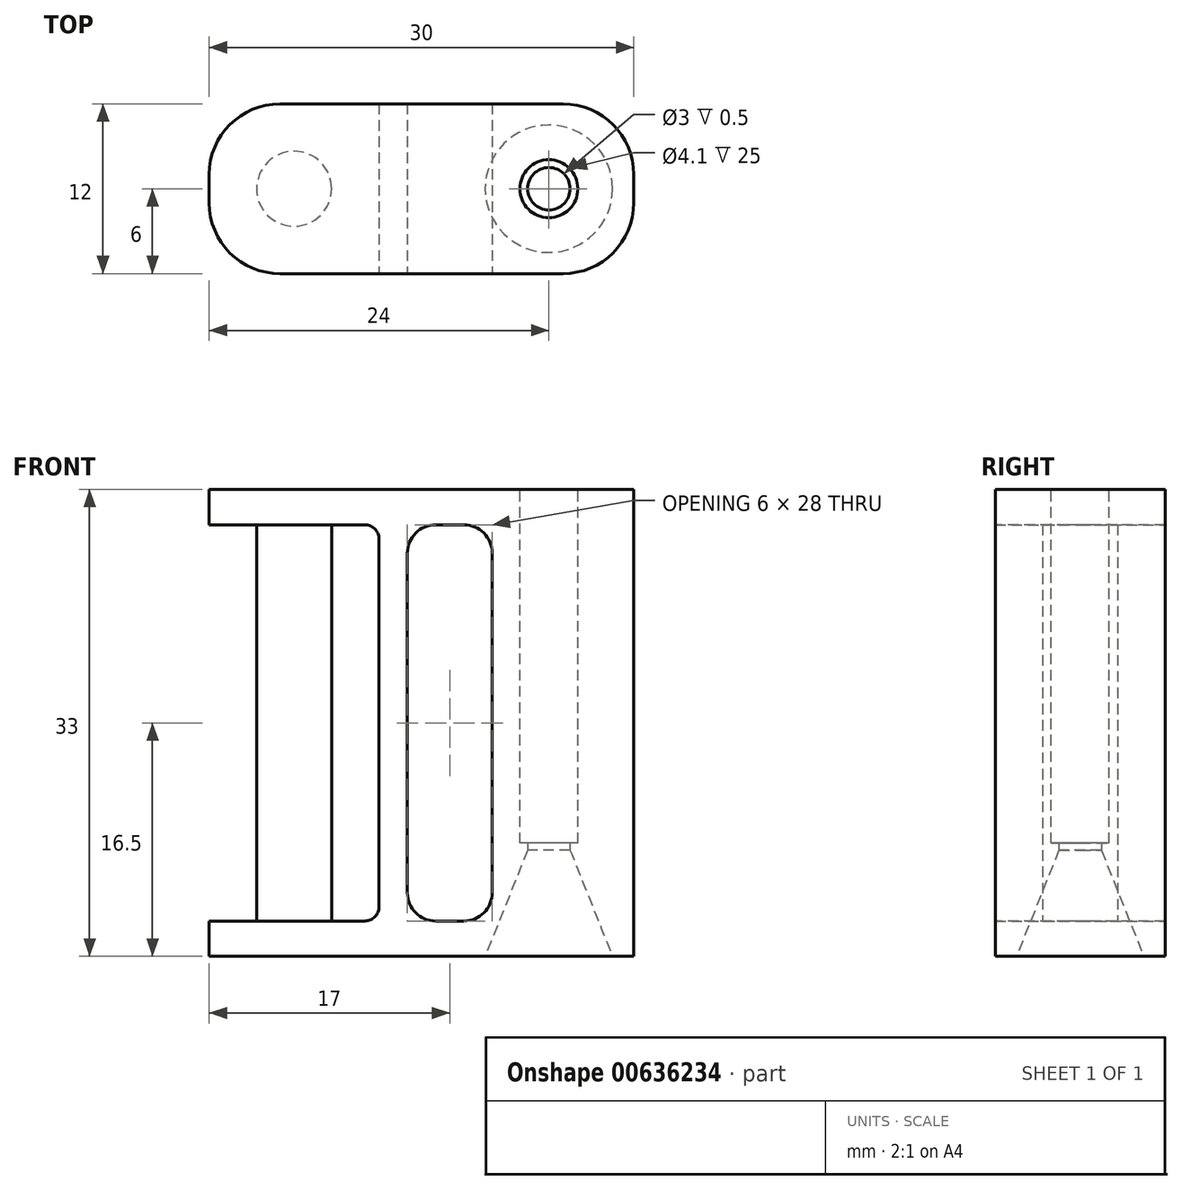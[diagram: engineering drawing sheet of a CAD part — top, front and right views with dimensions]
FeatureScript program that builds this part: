
annotation { "Feature Type Name" : "Feature", "Feature Type Description" : "" }
export const myFeature = defineFeature(function(context is Context, id is Id, definition is map)
    precondition{}
    {
        {
            var Q0;
            Q0=qCreatedBy(makeId("Top.planeOp"),FACE);
            var sketch = newSketch(context, id + "F0", { "sketchPlane" : qUnion([Q0])});
            skLineSegment(sketch, "E0.bottom", {"start": v(0, 0) * mm, "end": v(30, 0) * mm});
            skLineSegment(sketch, "E0.top", {"start": v(0, 12) * mm, "end": v(30, 12) * mm});
            skLineSegment(sketch, "E0.left", {"start": v(0, 0) * mm, "end": v(0, 12) * mm});
            skLineSegment(sketch, "E0.right", {"start": v(30, 0) * mm, "end": v(30, 12) * mm});
            skCircle(sketch, "E1", {"center": v(24, 6) * mm, "radius": 1.5 * mm});
            skSolve(sketch);
        }
        {
            var Q0;
            Q0=makeQuery(id+"F0.imprint","IMPRINT",FACE,{"disambiguationData":[TD([[makeQuery(id+"F0.imprint","IMPRINT",EDGE,{"derivedFrom":sQuery(id+"F0.wireOp",EDGE,"E0.bottom")}),1.0]])]});
            extrude(context, id + "F1", {"entities" : qUnion([Q0]), "depth" : 33 * mm, "offsetDistance" : 25 * mm});
        }
        {
            var Q0;
            Q0=makeQuery(id+"F1.opExtrude","SWEPT_FACE",FACE,{"disambiguationData":[OSD([sQuery(id+"F0.wireOp",EDGE,"E0.bottom")])]});
            var sketch = newSketch(context, id + "F2", { "sketchPlane" : qUnion([Q0])});
            skLineSegment(sketch, "E2.bottom", {"start": v(0, 30.5) * mm, "end": v(12, 30.5) * mm});
            skLineSegment(sketch, "E2.top", {"start": v(0, 2.5) * mm, "end": v(12, 2.5) * mm});
            skLineSegment(sketch, "E2.left", {"start": v(0, 30.5) * mm, "end": v(0, 2.5) * mm});
            skLineSegment(sketch, "E2.right", {"start": v(12, 30.5) * mm, "end": v(12, 2.5) * mm});
            skSolve(sketch);
        }
        {
            var Q0;
            Q0=makeQuery(id+"F2.imprint","IMPRINT",FACE,{"disambiguationData":[TD([[makeQuery(id+"F2.imprint","IMPRINT",EDGE,{"derivedFrom":sQuery(id+"F2.wireOp",EDGE,"E2.bottom")}),-1.0]])]});
            extrude(context, id + "F3", {"entities" : qUnion([Q0]), "operationType" : NewBodyOperationType.REMOVE, "oppositeDirection" : true, "depth" : 25 * mm, "offsetDistance" : 25 * mm});
        }
        {
            var Q0;
            Q0=makeQuery(id+"F3.boolean.opBoolean","COPY",FACE,{"derivedFrom":makeQuery(id+"F3.opExtrude","SWEPT_FACE",FACE,{"disambiguationData":[OSD([sQuery(id+"F2.wireOp",EDGE,"E2.top")])]})});
            var sketch = newSketch(context, id + "F4", { "sketchPlane" : qUnion([Q0])});
            skCircle(sketch, "E3", {"center": v(6, 6) * mm, "radius": 2.65 * mm});
            skSolve(sketch);
        }
        {
            var Q0;
            Q0=makeQuery(id+"F4.imprint","IMPRINT",FACE,{"disambiguationData":[TD([[makeQuery(id+"F4.imprint","IMPRINT",EDGE,{"derivedFrom":sQuery(id+"F4.wireOp",EDGE,"E3")}),1.0]])]});
            extrude(context, id + "F5", {"entities" : qUnion([Q0]), "operationType" : NewBodyOperationType.ADD, "depth" : 28.5 * mm, "offsetDistance" : 25 * mm});
        }
        {
            var Q0;
            {var subQ0=sQuery(id+"F0.wireOp",EDGE,"E0.bottom");var subQ1=sQuery(id+"F0.wireOp",EDGE,"E0.left");Q0=makeQuery(id+"F3.boolean.opBoolean","SPLIT",EDGE,{"disambiguationData":[TD([makeQuery(id+"F3.opExtrude","SWEPT_FACE",FACE,{"disambiguationData":[OSD([sQuery(id+"F2.wireOp",EDGE,"E2.top")])]})])],"derivedFrom":makeQuery(id+"F1.opExtrude","SWEPT_EDGE",EDGE,{"disambiguationData":[OSD([subQ0,subQ1])]})});}
            var Q1;
            {var subQ0=sQuery(id+"F0.wireOp",EDGE,"E0.bottom");var subQ1=sQuery(id+"F0.wireOp",EDGE,"E0.left");Q1=makeQuery(id+"F3.boolean.opBoolean","SPLIT",EDGE,{"disambiguationData":[TD([makeQuery(id+"F3.opExtrude","SWEPT_FACE",FACE,{"disambiguationData":[OSD([sQuery(id+"F2.wireOp",EDGE,"E2.bottom")])]})])],"derivedFrom":makeQuery(id+"F1.opExtrude","SWEPT_EDGE",EDGE,{"disambiguationData":[OSD([subQ0,subQ1])]})});}
            var Q2;
            {var subQ0=sQuery(id+"F0.wireOp",EDGE,"E0.left");var subQ1=sQuery(id+"F0.wireOp",EDGE,"E0.top");Q2=makeQuery(id+"F3.boolean.opBoolean","SPLIT",EDGE,{"disambiguationData":[TD([makeQuery(id+"F3.opExtrude","SWEPT_FACE",FACE,{"disambiguationData":[OSD([sQuery(id+"F2.wireOp",EDGE,"E2.bottom")])]})])],"derivedFrom":makeQuery(id+"F1.opExtrude","SWEPT_EDGE",EDGE,{"disambiguationData":[OSD([subQ1,subQ0])]})});}
            var Q3;
            {var subQ0=sQuery(id+"F0.wireOp",EDGE,"E0.left");var subQ1=sQuery(id+"F0.wireOp",EDGE,"E0.top");Q3=makeQuery(id+"F3.boolean.opBoolean","SPLIT",EDGE,{"disambiguationData":[TD([makeQuery(id+"F3.opExtrude","SWEPT_FACE",FACE,{"disambiguationData":[OSD([sQuery(id+"F2.wireOp",EDGE,"E2.top")])]})])],"derivedFrom":makeQuery(id+"F1.opExtrude","SWEPT_EDGE",EDGE,{"disambiguationData":[OSD([subQ1,subQ0])]})});}
            var Q4;
            Q4=makeQuery(id+"F1.opExtrude","SWEPT_EDGE",EDGE,{"disambiguationData":[OSD([sQuery(id+"F0.wireOp",EDGE,"E0.bottom"),sQuery(id+"F0.wireOp",EDGE,"E0.right")])]});
            var Q5;
            Q5=makeQuery(id+"F1.opExtrude","SWEPT_EDGE",EDGE,{"disambiguationData":[OSD([sQuery(id+"F0.wireOp",EDGE,"E0.top"),sQuery(id+"F0.wireOp",EDGE,"E0.right")])]});
            fillet(context, id + "F6", {"entities" : qUnion([Q0, Q1, Q2, Q3, Q4, Q5]), "radius" : 5 * mm, "tangentPropagation" : true, "allowEdgeOverflow" : false});
        }
        {
            var Q0;
            Q0=makeQuery(id+"F3.boolean.opBoolean","COPY",EDGE,{"derivedFrom":makeQuery(id+"F3.opExtrude","SWEPT_EDGE",EDGE,{"disambiguationData":[OSD([sQuery(id+"F2.wireOp",EDGE,"E2.top"),sQuery(id+"F2.wireOp",EDGE,"E2.right")])]})});
            var Q1;
            Q1=makeQuery(id+"F3.boolean.opBoolean","COPY",EDGE,{"derivedFrom":makeQuery(id+"F3.opExtrude","SWEPT_EDGE",EDGE,{"disambiguationData":[OSD([sQuery(id+"F2.wireOp",EDGE,"E2.bottom"),sQuery(id+"F2.wireOp",EDGE,"E2.right")])]})});
            fillet(context, id + "F7", {"entities" : qUnion([Q0, Q1]), "radius" : 1 * mm, "tangentPropagation" : true, "allowEdgeOverflow" : false});
        }
        {
            var Q0;
            Q0=makeQuery(id+"F1.opExtrude","CAP_FACE",FACE,{"disambiguationData":[OSD([sQuery(id+"F0.wireOp",EDGE,"E0.bottom"),sQuery(id+"F0.wireOp",EDGE,"E0.top"),sQuery(id+"F0.wireOp",EDGE,"E0.left"),sQuery(id+"F0.wireOp",EDGE,"E0.right"),sQuery(id+"F0.wireOp",EDGE,"E1")])],"isStart":false});
            var sketch = newSketch(context, id + "F8", { "sketchPlane" : qUnion([Q0])});
            skCircle(sketch, "E4", {"center": v(24, 6) * mm, "radius": 2.05 * mm});
            skSolve(sketch);
        }
        {
            var Q0;
            Q0=makeQuery(id+"F8.imprint","IMPRINT",FACE,{"disambiguationData":[TD([[makeQuery(id+"F8.imprint","IMPRINT",EDGE,{"derivedFrom":sQuery(id+"F8.wireOp",EDGE,"E4")}),1.0]])]});
            extrude(context, id + "F9", {"entities" : qUnion([Q0]), "operationType" : NewBodyOperationType.REMOVE, "oppositeDirection" : true, "depth" : 25 * mm, "offsetDistance" : 25 * mm});
        }
        {
            var Q0;
            Q0=makeQuery(id+"F1.opExtrude","CAP_EDGE",EDGE,{"disambiguationData":[OSD([sQuery(id+"F0.wireOp",EDGE,"E1")])],"isStart":true});
            chamfer(context, id + "F10", {"entities" : qUnion([Q0]), "chamferType" : ChamferType.TWO_OFFSETS, "width1" : 3 * mm, "oppositeDirection" : false, "width2" : 7.5 * mm, "tangentPropagation" : true});
        }
        {
            var Q0;
            Q0=makeQuery(id+"F1.opExtrude","SWEPT_FACE",FACE,{"disambiguationData":[OSD([sQuery(id+"F0.wireOp",EDGE,"E0.bottom")])]});
            var sketch = newSketch(context, id + "F11", { "sketchPlane" : qUnion([Q0])});
            skLineSegment(sketch, "E5.bottom", {"start": v(14, 30.5) * mm, "end": v(20, 30.5) * mm});
            skLineSegment(sketch, "E5.top", {"start": v(14, 2.5) * mm, "end": v(20, 2.5) * mm});
            skLineSegment(sketch, "E5.left", {"start": v(14, 30.5) * mm, "end": v(14, 2.5) * mm});
            skLineSegment(sketch, "E5.right", {"start": v(20, 30.5) * mm, "end": v(20, 2.5) * mm});
            skSolve(sketch);
        }
        {
            var Q0;
            Q0=makeQuery(id+"F11.imprint","IMPRINT",FACE,{"disambiguationData":[TD([[makeQuery(id+"F11.imprint","IMPRINT",EDGE,{"derivedFrom":sQuery(id+"F11.wireOp",EDGE,"E5.bottom")}),-1.0]])]});
            extrude(context, id + "F12", {"entities" : qUnion([Q0]), "operationType" : NewBodyOperationType.REMOVE, "oppositeDirection" : true, "depth" : 25 * mm, "offsetDistance" : 25 * mm});
        }
        {
            var Q0;
            Q0=makeQuery(id+"F12.boolean.opBoolean","COPY",EDGE,{"derivedFrom":makeQuery(id+"F12.opExtrude","SWEPT_EDGE",EDGE,{"disambiguationData":[OSD([sQuery(id+"F11.wireOp",EDGE,"E5.bottom"),sQuery(id+"F11.wireOp",EDGE,"E5.left")])]})});
            var Q1;
            Q1=makeQuery(id+"F12.boolean.opBoolean","COPY",EDGE,{"derivedFrom":makeQuery(id+"F12.opExtrude","SWEPT_EDGE",EDGE,{"disambiguationData":[OSD([sQuery(id+"F11.wireOp",EDGE,"E5.bottom"),sQuery(id+"F11.wireOp",EDGE,"E5.right")])]})});
            var Q2;
            Q2=makeQuery(id+"F12.boolean.opBoolean","COPY",EDGE,{"derivedFrom":makeQuery(id+"F12.opExtrude","SWEPT_EDGE",EDGE,{"disambiguationData":[OSD([sQuery(id+"F11.wireOp",EDGE,"E5.top"),sQuery(id+"F11.wireOp",EDGE,"E5.left")])]})});
            var Q3;
            Q3=makeQuery(id+"F12.boolean.opBoolean","COPY",EDGE,{"derivedFrom":makeQuery(id+"F12.opExtrude","SWEPT_EDGE",EDGE,{"disambiguationData":[OSD([sQuery(id+"F11.wireOp",EDGE,"E5.top"),sQuery(id+"F11.wireOp",EDGE,"E5.right")])]})});
            fillet(context, id + "F13", {"entities" : qUnion([Q0, Q1, Q2, Q3]), "radius" : 2 * mm, "tangentPropagation" : true, "allowEdgeOverflow" : false});
        }
    });
